FCSTD DOCUMENT  (FreeCAD 1.0R39109 (Git))
Label: Assembly
License: All rights reserved
LicenseURL: https://en.wikipedia.org/wiki/All_rights_reserved
objects: App::Link×4, App::FeaturePython×4, Assembly::JointGroup×1, Assembly::AssemblyObject×1
EXTERNAL_REF file=Base.FCStd obj=Body
EXTERNAL_REF file=first_link.FCStd obj=Body
EXTERNAL_REF file=second_link.FCStd obj=Body
EXTERNAL_REF file=third_link.FCStd obj=Body

FEATURE [App::Link] Base
  LinkedObject = -> <external Base.FCStd>#Body
FEATURE [App::FeaturePython] GroundedJoint  # Assembly grounded joint (typed FeaturePython)
  ObjectToGround = -> Base
FEATURE [App::Link] first_link
  LinkPlacement = pos=(0,0,160) rot=(0,0,-1;0.307823rad)
  LinkedObject = -> <external first_link.FCStd>#Body
  Placement = pos=(0,0,160) rot=(0,0,-1;0.307823rad)
FEATURE [App::Link] second_link
  LinkPlacement = pos=(11.3662,35.7507,307.303) rot=(-0.963574,0.149488,-0.221762;1.22088rad)
  LinkedObject = -> <external second_link.FCStd>#Body
  Placement = pos=(11.3662,35.7507,307.303) rot=(-0.963574,0.149488,-0.221762;1.22088rad)
FEATURE [App::Link] third_link
  LinkPlacement = pos=(-79.6232,-250.443,1315.28) rot=(0.983686,-0.152608,-0.095255;2.04029rad)
  LinkedObject = -> <external third_link.FCStd>#Body
  Placement = pos=(-79.6232,-250.443,1315.28) rot=(0.983686,-0.152608,-0.095255;2.04029rad)
FEATURE [App::FeaturePython] Joint  label="Revolute"  # Assembly joint (typed FeaturePython)
  Activated = true
  AngleMax = 0
  AngleMin = 0
  Detach1 = false
  Detach2 = false
  Distance = 0
  Distance2 = 0
  EnableAngleMax = false
  EnableAngleMin = false
  EnableLengthMax = false
  EnableLengthMin = false
  JointType = 1 (Revolute)
  LengthMax = 0
  LengthMin = 0
  Placement1 = pos=(0,0,160) rot=(0,0,1;0rad)
  Reference1 = -> Assembly [Base.Pad001.Edge27,Base.Pad001.Edge27]
  Reference2 = -> Assembly [first_link.Pad002.Edge26,first_link.Pad002.Edge26]
FEATURE [App::FeaturePython] Joint001  label="Revolute001"  # Assembly joint (typed FeaturePython)
  Activated = true
  AngleMax = 0
  AngleMin = 0
  Detach1 = false
  Detach2 = false
  Distance = 0
  Distance2 = 0
  EnableAngleMax = false
  EnableAngleMin = false
  EnableLengthMax = false
  EnableLengthMin = false
  JointType = 1 (Revolute)
  LengthMax = 0
  LengthMin = 0
  Placement1 = pos=(0,0,240) rot=(0.57735,0.57735,0.57735;2.0944rad)
  Placement2 = pos=(1.97e-14,-100,2.84e-14) rot=(0.57735,0.57735,0.57735;2.0944rad)
  Reference1 = -> Assembly [first_link.Pad002.Face12,first_link.Pad002.Face12]
  Reference2 = -> Assembly [second_link.Pad002.Face11,second_link.Pad002.Face11]
FEATURE [App::FeaturePython] Joint002  label="Revolute002"  # Assembly joint (typed FeaturePython)
  Activated = true
  AngleMax = 0
  AngleMin = 0
  Detach1 = false
  Detach2 = false
  Distance = 0
  Distance2 = 0
  EnableAngleMax = false
  EnableAngleMin = false
  EnableLengthMax = false
  EnableLengthMin = false
  JointType = 1 (Revolute)
  LengthMax = 0
  LengthMin = 0
  Placement1 = pos=(2e-16,-1040,1.421e-13) rot=(0.707107,0,0.707107;3.14159rad)
  Placement2 = pos=(7.3e-15,2.274e-13,100) rot=(0,1,0;1.5708rad)
  Reference1 = -> Assembly [second_link.Pad002.Face9,second_link.Pad002.Face9]
  Reference2 = -> Assembly [third_link.Cone.Face7,third_link.Cone.Face7]
FEATURE [Assembly::JointGroup] Joints
  Group = -> [GroundedJoint,Joint,Joint001,Joint002]
FEATURE [Assembly::AssemblyObject] Assembly
  Group = -> [Joints,Base,GroundedJoint,first_link,second_link,third_link,Joint,Joint001,Joint002]
  Origin = -> Origin
  Type = Assembly

RESOLVED EXTERNAL PARTS (link-assembly join: the EXTERNAL_REF files above that resolve inside this repo's crawl, each included once):
---- part Base.FCStd = doc fcstd_ada1d240111d ----
FCSTD DOCUMENT  (FreeCAD 1.0R39109 (Git))
Label: Base
License: All rights reserved
LicenseURL: https://en.wikipedia.org/wiki/All_rights_reserved
objects: Sketcher::SketchObject×2, PartDesign::Pad×2, PartDesign::Body×1
note: 11 computed .brp shape members not serialized (recipe doc carries the construction recipe); baked Part::Feature solids carry a one-line shape summary decoded from their .brp

FEATURE [Sketcher::SketchObject] Sketch
  ArcFitTolerance = 1e-06
  AttachmentSupport = -> [XY_Plane]
  FullyConstrained = true
  MakeInternals = false
  MapMode = 5
  sketch-geometry (12):
    g0: LineSegment StartX=-400 StartY=280 StartZ=0 EndX=-400 EndY=-280 EndZ=0
    g1: LineSegment StartX=-280 StartY=-400 StartZ=0 EndX=280 EndY=-400 EndZ=0
    g2: LineSegment StartX=400 StartY=-280 StartZ=0 EndX=400 EndY=280 EndZ=0
    g3: LineSegment StartX=280 StartY=400 StartZ=0 EndX=-280 EndY=400 EndZ=0
    g4: ArcOfCircle CenterX=-280 CenterY=280 CenterZ=0 NormalX=0 NormalY=0 NormalZ=1 AngleXU=0 Radius=120 StartAngle=1.5708 EndAngle=3.14159
    g5: GeomPoint [constr] X=-400 Y=400 Z=0
    g6: ArcOfCircle CenterX=-280 CenterY=-280 CenterZ=0 NormalX=0 NormalY=0 NormalZ=1 AngleXU=0 Radius=120 StartAngle=3.14159 EndAngle=4.71239
    g7: GeomPoint [constr] X=-400 Y=-400 Z=0
    g8: ArcOfCircle CenterX=280 CenterY=-280 CenterZ=0 NormalX=0 NormalY=0 NormalZ=1 AngleXU=0 Radius=120 StartAngle=4.71239 EndAngle=6.28319
    g9: GeomPoint [constr] X=400 Y=-400 Z=0
    g10: ArcOfCircle CenterX=280 CenterY=280 CenterZ=0 NormalX=0 NormalY=0 NormalZ=1 AngleXU=0 Radius=120 StartAngle=2e-16 EndAngle=1.5708
    g11: GeomPoint [constr] X=400 Y=400 Z=0
  constraints (28):
    c: Vertical(g0)
    c: Vertical(g2)
    c: Horizontal(g1)
    c: Horizontal(g3)
    c: DistanceX(g5,g11) = 800
    c: DistanceY(g9,g11) = 800
    c: DistanceX(g-1,g11) = 400
    c: DistanceY(g-1,g11) = 400
    c: PointOnObject(g5,g3)
    c: PointOnObject(g5,g0)
    c: Tangent(g3,g4) = -1.5708
    c: Tangent(g0,g4) = -1.5708
    c: PointOnObject(g7,g0)
    c: PointOnObject(g7,g1)
    c: Tangent(g0,g6) = -1.5708
    c: Tangent(g1,g6) = -1.5708
    c: PointOnObject(g9,g2)
    c: PointOnObject(g9,g1)
    c: Tangent(g2,g8) = -1.5708
    c: Tangent(g1,g8) = -1.5708
    c: PointOnObject(g11,g2)
    c: PointOnObject(g11,g3)
    c: Tangent(g2,g10) = -1.5708
    c: Tangent(g3,g10) = -1.5708
    c: Equal(g4,g10)
    c: Equal(g4,g8)
    c: Equal(g4,g6)
    c: Radius(g4) = 120
FEATURE [PartDesign::Pad] Pad
  Direction = (0,0,1)
  Length = 80
  Length2 = 10
  Profile = -> Sketch
  ReferenceAxis = -> Sketch [N_Axis]
  Refine = true
  Suppressed = false
  Type = 0
FEATURE [Sketcher::SketchObject] Sketch001
  ArcFitTolerance = 1e-06
  AttachmentSupport = -> [Pad]
  FullyConstrained = true
  MakeInternals = false
  MapMode = 5
  Placement = pos=(0,0,80) rot=(0,0,1;0rad)
  sketch-geometry (1):
    g0: Circle CenterX=0 CenterY=0 CenterZ=0 NormalX=0 NormalY=0 NormalZ=1 AngleXU=0 Radius=200
  constraints (2):
    c: Diameter(g0) = 400
    c: Coincident(g0,g-1)
FEATURE [PartDesign::Pad] Pad001
  BaseFeature = -> Pad
  Direction = (0,0,1)
  Length = 80
  Length2 = 10
  Profile = -> Sketch001
  ReferenceAxis = -> Sketch001 [N_Axis]
  Refine = true
  Suppressed = false
  Type = 0
FEATURE [PartDesign::Body] Body  label="Base"
  AllowCompound = false
  Group = -> [Sketch,Pad,Sketch001,Pad001]
  Origin = -> Origin
  Tip = -> Pad001
---- part first_link.FCStd = doc fcstd_30c32fcff5f2 ----
FCSTD DOCUMENT  (FreeCAD 1.0R39109 (Git))
Label: first_link
License: All rights reserved
LicenseURL: https://en.wikipedia.org/wiki/All_rights_reserved
objects: Sketcher::SketchObject×3, PartDesign::Pad×3, PartDesign::Fillet×1, PartDesign::Body×1
note: 19 computed .brp shape members not serialized (recipe doc carries the construction recipe); baked Part::Feature solids carry a one-line shape summary decoded from their .brp

FEATURE [Sketcher::SketchObject] Sketch
  ArcFitTolerance = 1e-06
  AttachmentSupport = -> [XY_Plane]
  FullyConstrained = true
  MakeInternals = false
  MapMode = 5
  sketch-geometry (1):
    g0: Circle CenterX=0 CenterY=0 CenterZ=0 NormalX=0 NormalY=0 NormalZ=1 AngleXU=0 Radius=200
  constraints (2):
    c: Diameter(g0) = 400
    c: Coincident(g0,g-1)
FEATURE [PartDesign::Pad] Pad
  Direction = (0,0,1)
  Length = 100
  Length2 = 10
  Profile = -> Sketch
  ReferenceAxis = -> Sketch [N_Axis]
  Refine = true
  Suppressed = false
  Type = 0
FEATURE [Sketcher::SketchObject] Sketch001
  ArcFitTolerance = 1e-06
  AttachmentSupport = -> [Pad]
  FullyConstrained = true
  MakeInternals = false
  MapMode = 5
  Placement = pos=(0,0,100) rot=(0,0,1;0rad)
  sketch-geometry (8):
    g0: LineSegment StartX=-150 StartY=125 StartZ=0 EndX=-150 EndY=-125 EndZ=0
    g1: LineSegment StartX=-150 StartY=-125 StartZ=0 EndX=-100 EndY=-125 EndZ=0
    g2: LineSegment StartX=-100 StartY=-125 StartZ=0 EndX=-100 EndY=125 EndZ=0
    g3: LineSegment StartX=-100 StartY=125 StartZ=0 EndX=-150 EndY=125 EndZ=0
    g4: LineSegment StartX=100 StartY=125 StartZ=0 EndX=100 EndY=-125 EndZ=0
    g5: LineSegment StartX=100 StartY=-125 StartZ=0 EndX=150 EndY=-125 EndZ=0
    g6: LineSegment StartX=150 StartY=-125 StartZ=0 EndX=150 EndY=125 EndZ=0
    g7: LineSegment StartX=150 StartY=125 StartZ=0 EndX=100 EndY=125 EndZ=0
  constraints (24):
    c: Coincident(g0,g1)
    c: Coincident(g1,g2)
    c: Coincident(g2,g3)
    c: Coincident(g3,g0)
    c: Vertical(g0)
    c: Vertical(g2)
    c: Horizontal(g1)
    c: Horizontal(g3)
    c: DistanceX(g3,g3) = 50
    c: DistanceY(g0,g0) = 250
    c: DistanceX(g2,g-1) = 100
    c: DistanceY(g-1,g2) = 125
    c: Coincident(g4,g5)
    c: Coincident(g5,g6)
    c: Coincident(g6,g7)
    c: Coincident(g7,g4)
    c: Vertical(g4)
    c: Vertical(g6)
    c: Horizontal(g5)
    c: Horizontal(g7)
    c: DistanceX(g7,g7) = 50
    c: DistanceY(g4,g4) = 250
    c: DistanceX(g-1,g4) = 100
    c: DistanceY(g-1,g4) = 125
FEATURE [PartDesign::Pad] Pad001
  BaseFeature = -> Pad
  Direction = (0,0,1)
  Length = 220
  Length2 = 10
  Profile = -> Sketch001
  ReferenceAxis = -> Sketch001 [N_Axis]
  Refine = true
  Suppressed = false
  Type = 0
FEATURE [PartDesign::Fillet] Fillet
  Base = -> Pad001 [Edge16,Edge24,Edge27,Edge19]
  BaseFeature = -> Pad001
  Radius = 120
  Refine = true
  SupportTransform = false
  Suppressed = false
  UseAllEdges = false
FEATURE [Sketcher::SketchObject] Sketch002
  ArcFitTolerance = 1e-06
  AttachmentSupport = -> [Fillet]
  FullyConstrained = true
  MakeInternals = false
  MapMode = 5
  Placement = pos=(150,0,0) rot=(0.57735,0.57735,0.57735;2.0944rad)
  sketch-geometry (1):
    g0: Circle CenterX=0 CenterY=240 CenterZ=0 NormalX=0 NormalY=0 NormalZ=1 AngleXU=0 Radius=50
  constraints (3):
    c: Diameter(g0) = 100
    c: DistanceY(g-1,g0) = 240
    c: DistanceX(g-1,g0) = 0
FEATURE [PartDesign::Pad] Pad002
  BaseFeature = -> Fillet
  Direction = (1,0,0)
  Length = 300
  Length2 = 10
  Profile = -> Sketch002
  ReferenceAxis = -> Sketch002 [N_Axis]
  Refine = true
  Reversed = true
  Suppressed = false
  Type = 0
FEATURE [PartDesign::Body] Body  label="first_link"
  AllowCompound = false
  Group = -> [Sketch,Pad,Sketch001,Pad001,Fillet,Sketch002,Pad002]
  Origin = -> Origin
  Tip = -> Pad002
---- part second_link.FCStd = doc fcstd_42b4278a60ad ----
FCSTD DOCUMENT  (FreeCAD 1.0R39109 (Git))
Label: second_link
License: All rights reserved
LicenseURL: https://en.wikipedia.org/wiki/All_rights_reserved
objects: Sketcher::SketchObject×4, PartDesign::Pad×3, PartDesign::Hole×1, PartDesign::Body×1
note: 21 computed .brp shape members not serialized (recipe doc carries the construction recipe); baked Part::Feature solids carry a one-line shape summary decoded from their .brp

FEATURE [Sketcher::SketchObject] Sketch
  ArcFitTolerance = 1e-06
  AttachmentSupport = -> [XZ_Plane]
  FullyConstrained = true
  MakeInternals = false
  MapMode = 5
  Placement = pos=(0,0,0) rot=(1,0,0;1.5708rad)
  sketch-geometry (4):
    g0: LineSegment StartX=-75 StartY=80 StartZ=0 EndX=-75 EndY=-80 EndZ=0
    g1: LineSegment StartX=-75 StartY=-80 StartZ=0 EndX=75 EndY=-80 EndZ=0
    g2: LineSegment StartX=75 StartY=-80 StartZ=0 EndX=75 EndY=80 EndZ=0
    g3: LineSegment StartX=75 StartY=80 StartZ=0 EndX=-75 EndY=80 EndZ=0
  constraints (12):
    c: Coincident(g0,g1)
    c: Coincident(g1,g2)
    c: Coincident(g2,g3)
    c: Coincident(g3,g0)
    c: Vertical(g0)
    c: Vertical(g2)
    c: Horizontal(g1)
    c: Horizontal(g3)
    c: DistanceX(g3,g3) = 150
    c: DistanceY(g0,g0) = 160
    c: DistanceY(g-1,g2) = 80
    c: DistanceX(g-1,g2) = 75
FEATURE [PartDesign::Pad] Pad
  Direction = (0,-1,2e-16)
  Length = 900
  Length2 = 10
  Placement = pos=(0,0,0) rot=(1,0,0;1.5708rad)
  Profile = -> Sketch
  ReferenceAxis = -> Sketch [N_Axis]
  Refine = true
  Suppressed = false
  Type = 0
FEATURE [Sketcher::SketchObject] Sketch001
  ArcFitTolerance = 1e-06
  AttachmentSupport = -> [Pad]
  FullyConstrained = true
  MakeInternals = false
  MapMode = 5
  Placement = pos=(75,0,0) rot=(0.707107,0,0.707107;3.14159rad)
  sketch-geometry (1):
    g0: Circle CenterX=0 CenterY=100 CenterZ=0 NormalX=0 NormalY=0 NormalZ=1 AngleXU=0 Radius=50
  constraints (3):
    c: PointOnObject(g0,g-2)
    c: Radius(g0) = 50
    c: DistanceY(g-1,g0) = 100
FEATURE [PartDesign::Hole] Hole
  BaseFeature = -> Pad
  CustomThreadClearance = 0
  Depth = 150
  DepthType = 0
  Diameter = 100
  DrillForDepth = false
  DrillPoint = 1
  DrillPointAngle = 118
  HoleCutCountersinkAngle = 90
  HoleCutCustomValues = false
  HoleCutDepth = 0
  HoleCutDiameter = 6.1
  HoleCutType = 0
  ModelThread = false
  Placement = pos=(0,0,0) rot=(1,0,0;1.5708rad)
  Profile = -> Sketch001 [Edge1]
  Refine = true
  Suppressed = false
  Tapered = false
  TaperedAngle = 90
  ThreadClass = 0
  ThreadDepth = 150
  ThreadDepthType = 0
  ThreadDirection = 0
  ThreadFit = 0
  ThreadSize = 0
  ThreadType = 0
  Threaded = false
  UseCustomThreadClearance = false
FEATURE [Sketcher::SketchObject] Sketch002
  ArcFitTolerance = 1e-06
  AttachmentSupport = -> [Hole]
  ExternalGeometry = -> [Hole]
  FullyConstrained = true
  MakeInternals = false
  MapMode = 5
  Placement = pos=(0,-900,0) rot=(1,0,0;1.5708rad)
  sketch-geometry (8):
    g0: LineSegment StartX=-75 StartY=80 StartZ=0 EndX=-75 EndY=-80 EndZ=0
    g1: LineSegment StartX=-75 StartY=-80 StartZ=0 EndX=-45 EndY=-80 EndZ=0
    g2: LineSegment StartX=-45 StartY=-80 StartZ=0 EndX=-45 EndY=80 EndZ=0
    g3: LineSegment StartX=-45 StartY=80 StartZ=0 EndX=-75 EndY=80 EndZ=0
    g4: LineSegment StartX=75 StartY=80 StartZ=0 EndX=45 EndY=80 EndZ=0
    g5: LineSegment StartX=45 StartY=80 StartZ=0 EndX=45 EndY=-80 EndZ=0
    g6: LineSegment StartX=45 StartY=-80 StartZ=0 EndX=75 EndY=-80 EndZ=0
    g7: LineSegment StartX=75 StartY=-80 StartZ=0 EndX=75 EndY=80 EndZ=0
  constraints (22):
    c: Coincident(g0,g1)
    c: Coincident(g1,g2)
    c: Coincident(g2,g3)
    c: Coincident(g3,g0)
    c: Vertical(g0)
    c: Vertical(g2)
    c: Horizontal(g1)
    c: Horizontal(g3)
    c: Coincident(g0,g-3)
    c: Coincident(g4,g5)
    c: Coincident(g5,g6)
    c: Coincident(g6,g7)
    c: Coincident(g7,g4)
    c: Horizontal(g4)
    c: Horizontal(g6)
    c: Vertical(g5)
    c: Vertical(g7)
    c: Coincident(g4,g-4)
    c: DistanceY(g2,g2) = 160
    c: DistanceX(g3,g3) = 30
    c: DistanceY(g5,g5) = 160
    c: DistanceX(g4,g4) = 30
FEATURE [PartDesign::Pad] Pad001
  BaseFeature = -> Hole
  Direction = (0,-1,2e-16)
  Length = 200
  Length2 = 10
  Placement = pos=(0,0,0) rot=(1,0,0;1.5708rad)
  Profile = -> Sketch002
  ReferenceAxis = -> Sketch002 [N_Axis]
  Refine = true
  Suppressed = false
  Type = 0
FEATURE [Sketcher::SketchObject] Sketch003
  ArcFitTolerance = 1e-06
  AttachmentSupport = -> [Pad001]
  ExternalGeometry = -> [Pad001]
  FullyConstrained = true
  MakeInternals = false
  MapMode = 5
  Placement = pos=(75,0,0) rot=(0.707107,0,0.707107;3.14159rad)
  sketch-geometry (1):
    g0: Circle CenterX=0 CenterY=1040 CenterZ=0 NormalX=0 NormalY=0 NormalZ=1 AngleXU=0 Radius=30
  constraints (3):
    c: Diameter(g0) = 60
    c: PointOnObject(g0,g-2)
    c: DistanceY(g0,g-4) = 60
FEATURE [PartDesign::Pad] Pad002
  BaseFeature = -> Pad001
  Direction = (1,0,-2e-16)
  Length = 150
  Length2 = 10
  Placement = pos=(0,0,0) rot=(1,0,0;1.5708rad)
  Profile = -> Sketch003 [Edge1]
  ReferenceAxis = -> Sketch003 [N_Axis]
  Refine = true
  Reversed = true
  Suppressed = false
  Type = 0
FEATURE [PartDesign::Body] Body  label="second_link"
  AllowCompound = false
  Group = -> [Sketch,Pad,Sketch001,Hole,Sketch002,Pad001,Sketch003,Pad002]
  Origin = -> Origin
  Tip = -> Pad002
---- part third_link.FCStd = doc fcstd_350540018f04 ----
FCSTD DOCUMENT  (FreeCAD 1.0R39109 (Git))
Label: third_link
License: All rights reserved
LicenseURL: https://en.wikipedia.org/wiki/All_rights_reserved
objects: Sketcher::SketchObject×2, PartDesign::Pad×1, PartDesign::Hole×1, PartDesign::AdditiveCone×1, PartDesign::Body×1
note: 14 computed .brp shape members not serialized (recipe doc carries the construction recipe); baked Part::Feature solids carry a one-line shape summary decoded from their .brp

FEATURE [Sketcher::SketchObject] Sketch
  ArcFitTolerance = 1e-06
  AttachmentSupport = -> [XY_Plane]
  FullyConstrained = true
  MakeInternals = false
  MapMode = 5
  sketch-geometry (4):
    g0: LineSegment StartX=-40 StartY=90 StartZ=0 EndX=-40 EndY=-90 EndZ=0
    g1: LineSegment StartX=-40 StartY=-90 StartZ=0 EndX=40 EndY=-90 EndZ=0
    g2: LineSegment StartX=40 StartY=-90 StartZ=0 EndX=40 EndY=90 EndZ=0
    g3: LineSegment StartX=40 StartY=90 StartZ=0 EndX=-40 EndY=90 EndZ=0
  constraints (12):
    c: Coincident(g0,g1)
    c: Coincident(g1,g2)
    c: Coincident(g2,g3)
    c: Coincident(g3,g0)
    c: Vertical(g0)
    c: Vertical(g2)
    c: Horizontal(g1)
    c: Horizontal(g3)
    c: DistanceX(g3,g3) = 80
    c: DistanceY(g0,g0) = 180
    c: DistanceY(g-1,g2) = 90
    c: DistanceX(g2) = 40
FEATURE [PartDesign::Pad] Pad
  Direction = (0,0,1)
  Length = 600
  Length2 = 10
  Profile = -> Sketch
  ReferenceAxis = -> Sketch [N_Axis]
  Refine = true
  Suppressed = false
  Type = 0
FEATURE [Sketcher::SketchObject] Sketch001
  ArcFitTolerance = 1e-06
  AttachmentSupport = -> [Pad]
  FullyConstrained = true
  MakeInternals = false
  MapMode = 5
  Placement = pos=(40,0,0) rot=(0.57735,0.57735,0.57735;2.0944rad)
  sketch-geometry (1):
    g0: Circle CenterX=0 CenterY=100 CenterZ=0 NormalX=0 NormalY=0 NormalZ=1 AngleXU=0 Radius=30
  constraints (3):
    c: Diameter(g0) = 60
    c: PointOnObject(g0,g-2)
    c: DistanceY(g-1,g0) = 100
FEATURE [PartDesign::Hole] Hole
  BaseFeature = -> Pad
  CustomThreadClearance = 0
  Depth = 80
  DepthType = 0
  Diameter = 60
  DrillForDepth = false
  DrillPoint = 1
  DrillPointAngle = 118
  HoleCutCountersinkAngle = 90
  HoleCutCustomValues = false
  HoleCutDepth = 0
  HoleCutDiameter = 6.1
  HoleCutType = 0
  ModelThread = false
  Profile = -> Sketch001
  Refine = true
  Suppressed = false
  Tapered = false
  TaperedAngle = 90
  ThreadClass = 0
  ThreadDepth = 80
  ThreadDepthType = 0
  ThreadDirection = 0
  ThreadFit = 0
  ThreadSize = 0
  ThreadType = 0
  Threaded = false
  UseCustomThreadClearance = false
FEATURE [PartDesign::AdditiveCone] Cone
  Angle = 360
  AttacherType = Attacher::AttachEngine3D
  AttachmentOffset = pos=(0,0,150) rot=(1,0,0;3.14159rad)
  AttachmentSupport = -> [Hole]
  BaseFeature = -> Hole
  Height = 150
  MapMode = 5
  Placement = pos=(0,0,750) rot=(1,0,0;3.14159rad)
  Radius1 = 0
  Radius2 = 40
  Refine = true
  Suppressed = false
FEATURE [PartDesign::Body] Body  label="third_link"
  AllowCompound = false
  Group = -> [Sketch,Pad,Sketch001,Hole,Cone]
  Origin = -> Origin
  Tip = -> Cone
